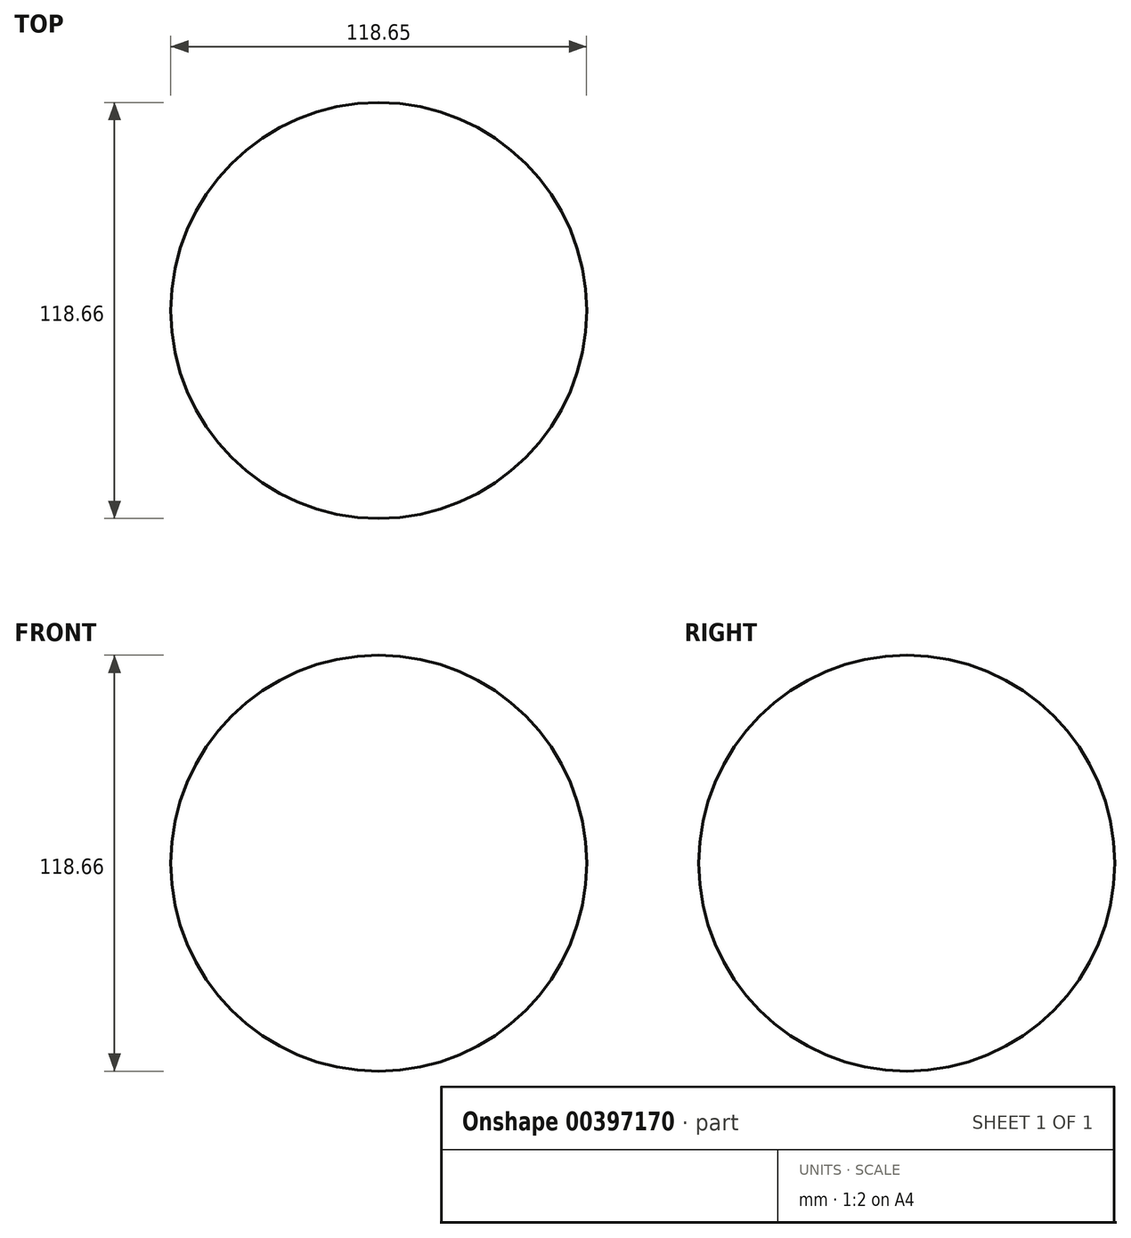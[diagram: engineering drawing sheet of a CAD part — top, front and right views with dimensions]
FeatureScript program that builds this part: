
annotation { "Feature Type Name" : "Feature", "Feature Type Description" : "" }
export const myFeature = defineFeature(function(context is Context, id is Id, definition is map)
    precondition{}
    {
        {
            var Q0;
            Q0=qCreatedBy(makeId("Top.planeOp"),FACE);
            var sketch = newSketch(context, id + "F0", { "sketchPlane" : qUnion([Q0])});
            skCircle(sketch, "E0", {"center": v(-8.2, 0) * mm, "radius": 59.33 * mm});
            skLineSegment(sketch, "E1", {"start": v(-8.2, 0) * mm, "end": v(51.13, 0) * mm});
            skLineSegment(sketch, "E2", {"start": v(51.13, 0) * mm, "end": v(-67.52, 0) * mm});
            skSolve(sketch);
        }
        {
            var Q0;
            {var subQ0=sQuery(id+"F0.wireOp",EDGE,"E2");var subQ4=makeQuery(id+"F0.imprint","IMPRINT",VERTEX,{"derivedFrom":subQ0});Q0=makeQuery(id+"F0.imprint","IMPRINT",FACE,{"disambiguationData":[TD([[makeQuery(id+"F0.imprint","IMPRINT",EDGE,{"disambiguationData":[TD([[subQ4,1.0]])],"derivedFrom":subQ0}),1.0]])]});}
            var Q1;
            Q1=sQuery(id+"F0.wireOp",EDGE,"E2");
            revolve(context, id + "F1", {"surfaceOperationType" : NewSurfaceOperationType.NEW, "entities" : qUnion([Q0]), "axis" : qUnion([Q1]), "revolveType" : RevolveType.FULL});
        }
    });
